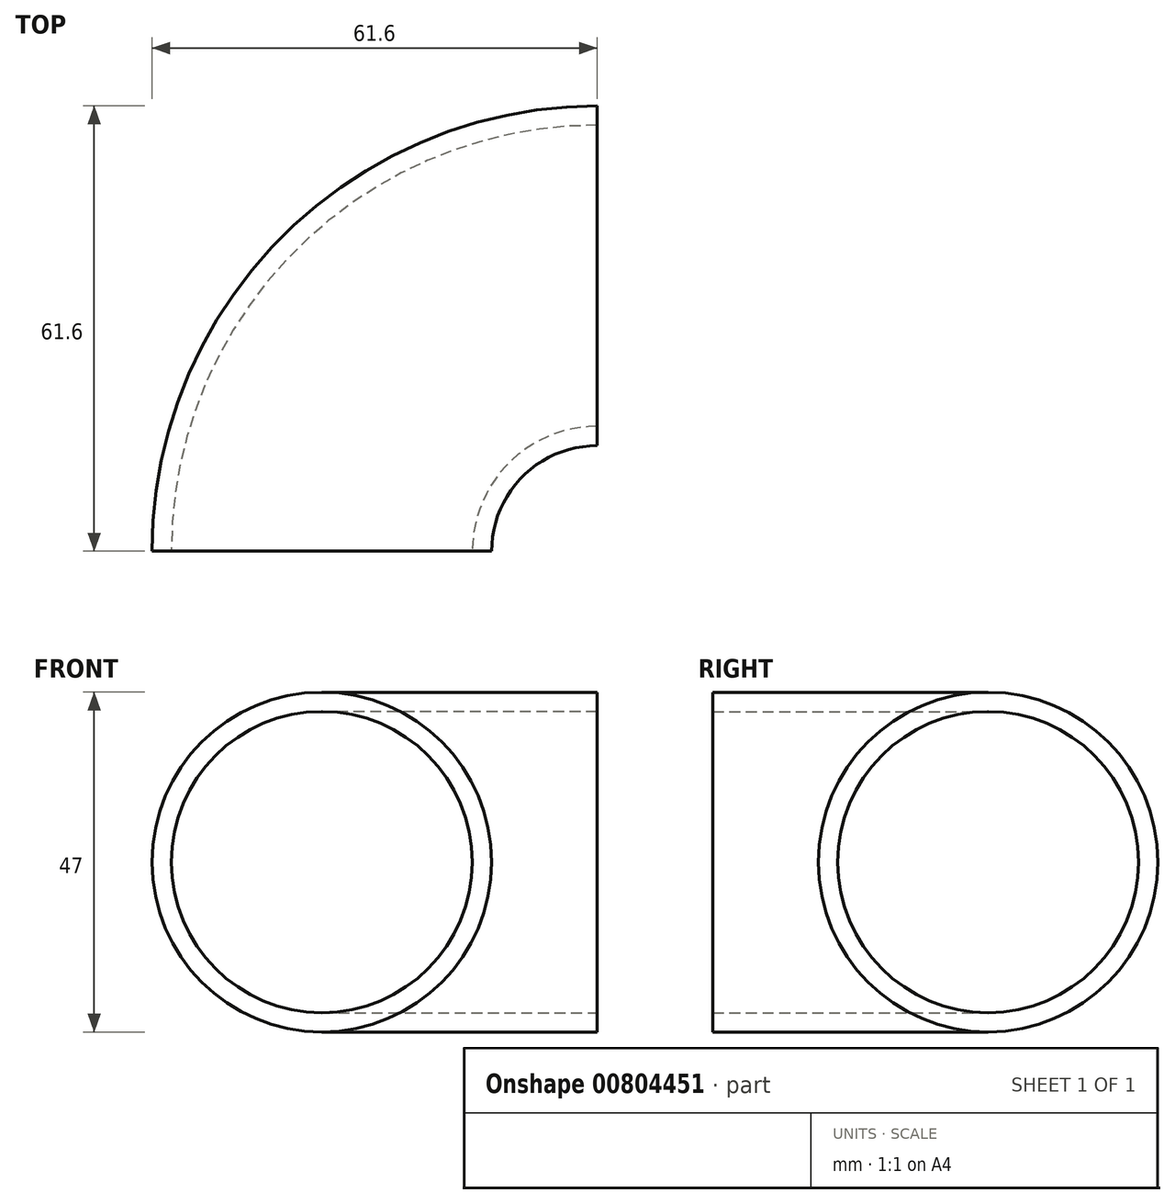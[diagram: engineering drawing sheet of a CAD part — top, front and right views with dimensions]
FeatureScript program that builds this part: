
annotation { "Feature Type Name" : "Feature", "Feature Type Description" : "" }
export const myFeature = defineFeature(function(context is Context, id is Id, definition is map)
    precondition{}
    {
        {
            var Q0;
            Q0=qCreatedBy(makeId("Top.planeOp"),FACE);
            var sketch = newSketch(context, id + "F0", { "sketchPlane" : qUnion([Q0])});
            skArc(sketch, "E0", {"start": v(0, 38.1) * mm, "mid": v(-26.94, 26.94) * mm, "end": v(-38.1, 0) * mm});
            skSolve(sketch);
        }
        {
            var Q0;
            Q0=qCreatedBy(makeId("Front.planeOp"),FACE);
            var sketch = newSketch(context, id + "F1", { "sketchPlane" : qUnion([Q0])});
            skLineSegment(sketch, "E1.0", {"start": v(0, 0) * mm, "end": v(-38.1, 0) * mm});
            skCircle(sketch, "E2", {"center": v(-38.1, 0) * mm, "radius": 23.5 * mm});
            skCircle(sketch, "E3", {"center": v(-38.1, 0) * mm, "radius": 20.83 * mm});
            skSolve(sketch);
        }
        {
            var Q0;
            Q0=makeQuery(id+"F1.imprint","IMPRINT",FACE,{"disambiguationData":[TD([[makeQuery(id+"F1.imprint","IMPRINT",EDGE,{"derivedFrom":sQuery(id+"F1.wireOp",EDGE,"E2")}),1.0]])]});
            var Q1;
            Q1=sQuery(id+"F0.wireOp",EDGE,"E0");
            sweep(context, id + "F2", {"profiles" : qUnion([Q0]), "path" : qUnion([Q1])});
        }
    });
